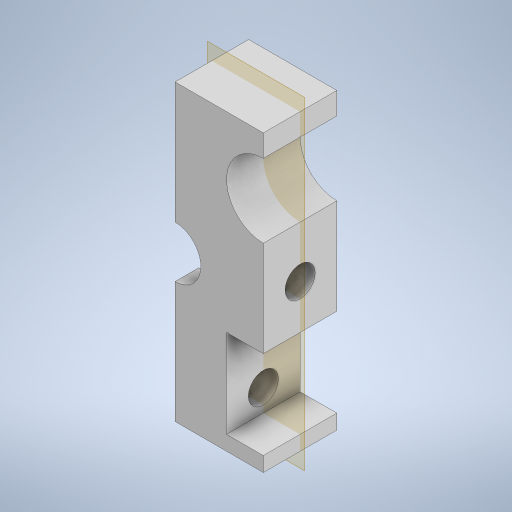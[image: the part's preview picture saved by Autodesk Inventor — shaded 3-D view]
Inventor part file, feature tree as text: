
AUTODESK INVENTOR PART (.ipt)
format: ipt  version: 2023 (Build 270158000, 158)  size: 331,776 bytes
history: native  units: mm
features: extrude x7, sketch x7, plane x1
ambient origin geometry x8: Origin, YZ Plane, XZ Plane, XY Plane, X Axis, Y Axis, Z Axis, Center Point
bodies: Solid1 (feature_tree)
feature tree (15):
  extrude  "Extrusion1"  Depth=20.0mm
  plane  "Work Plane1"
  extrude  "Extrusion2"  Depth=2.0mm
  extrude  "Extrusion3"  Depth=4.0mm
  extrude  "Extrusion4"  Depth=5.0mm TaperAngle=0.0deg
  extrude  "Extrusion5"  Depth=5.0mm TaperAngle=0.0deg
  extrude  "Extrusion6"  Depth=8.0mm TaperAngle=0.0deg
  extrude  "Extrusion7"  Depth=10.0mm
  sketch  "Sketch1"  dims[d0=20.0mm d1=20.0mm]
  sketch  "Sketch2"  dims[d2=4.0mm d6=2.0mm]
  sketch  "Sketch3"  dims[d7=2.0mm d8=4.0mm]
  sketch  "Sketch4"  dims[d9=2.0mm d10=5.0mm d11=0.0mm]
  sketch  "Sketch5"  dims[d12=5.0mm d13=1.8mm d14=0.0mm]
  sketch  "Sketch6"  dims[d15=3.5mm d16=8.0mm d17=0.0mm]
  sketch  "Sketch7"  dims[d18=2.05mm d19=2.05mm d20=2.5mm d21=2.5mm d22=2.5mm d23=2.5mm d24=25.0mm d25=0.0mm d30=5.0mm d31=0.0mm d32=2.5mm d33=1.0mm d34=6.0mm d35=5.0mm d36=4.0mm d37=5.0mm d38=0.0mm d39=2.5mm d40=10.0mm d41=2.05mm d42=12.0mm d43=0.0mm d44=6.0mm]
